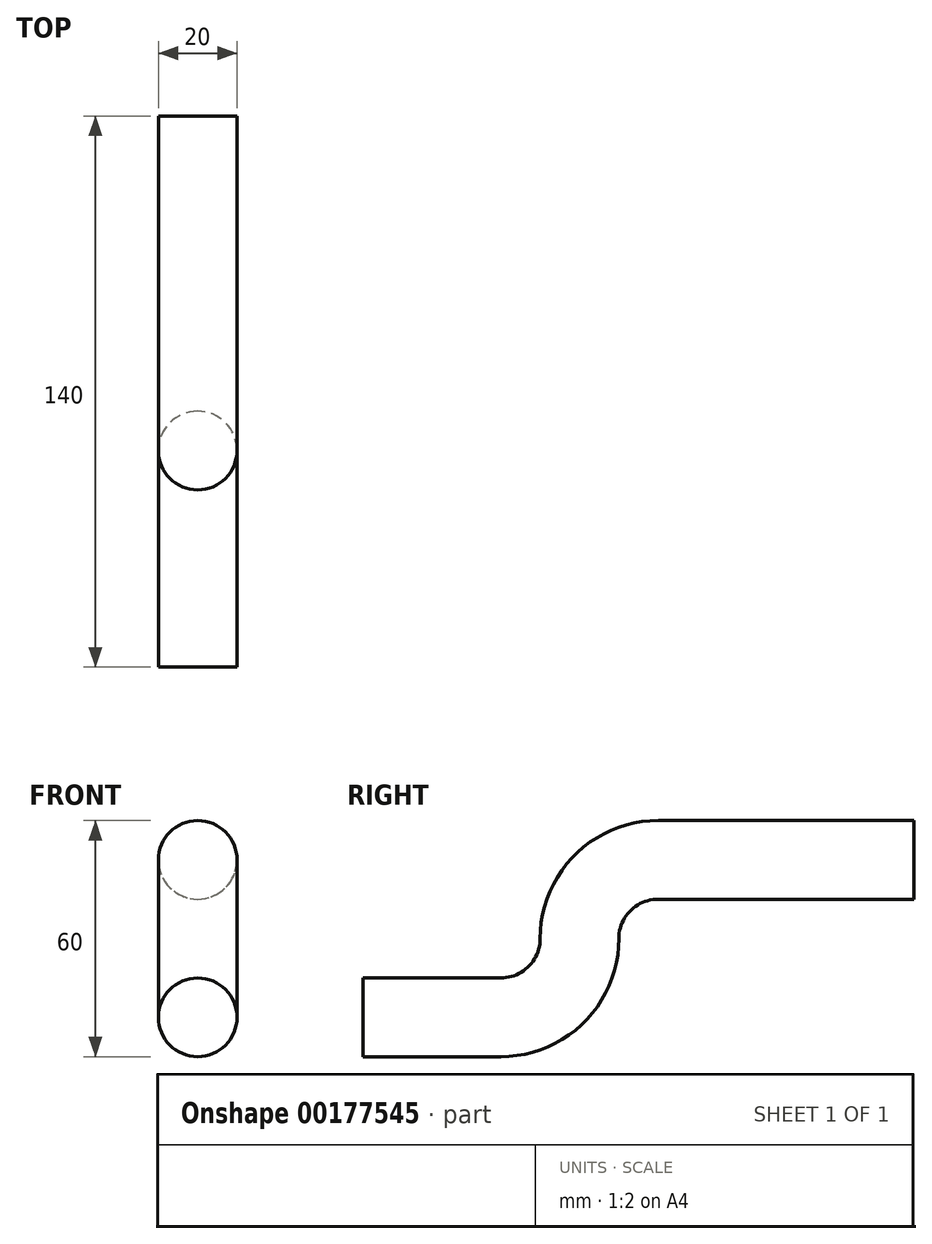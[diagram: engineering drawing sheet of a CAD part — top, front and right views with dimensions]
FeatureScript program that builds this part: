
annotation { "Feature Type Name" : "Feature", "Feature Type Description" : "" }
export const myFeature = defineFeature(function(context is Context, id is Id, definition is map)
    precondition{}
    {
        {
            var Q0;
            Q0=qCreatedBy(makeId("Front.planeOp"),FACE);
            var sketch = newSketch(context, id + "F0", { "sketchPlane" : qUnion([Q0])});
            skCircle(sketch, "E0", {"center": v(0, 0) * mm, "radius": 10 * mm});
            skSolve(sketch);
        }
        {
            var Q0;
            Q0=qCreatedBy(makeId("Right.planeOp"),FACE);
            var sketch = newSketch(context, id + "F1", { "sketchPlane" : qUnion([Q0])});
            skLineSegment(sketch, "E1", {"start": v(0, 0) * mm, "end": v(35, 0) * mm});
            skArc(sketch, "E2", {"start": v(35, 0) * mm, "mid": v(49.14, 5.86) * mm, "end": v(55, 20) * mm});
            skArc(sketch, "E3", {"start": v(55, 20) * mm, "mid": v(60.86, 34.14) * mm, "end": v(75, 40) * mm});
            skLineSegment(sketch, "E4", {"start": v(75, 40) * mm, "end": v(140, 40) * mm});
            skSolve(sketch);
        }
        {
            var Q0;
            Q0 = qSketchRegion(id + "F0", true);
            var Q1;
            Q1=sQuery(id+"F1.wireOp",EDGE,"E1");
            var Q2;
            Q2=sQuery(id+"F1.wireOp",EDGE,"E2");
            var Q3;
            Q3=sQuery(id+"F1.wireOp",EDGE,"E3");
            var Q4;
            Q4=sQuery(id+"F1.wireOp",EDGE,"E4");
            sweep(context, id + "F2", {"profiles" : qUnion([Q0]), "path" : qUnion([Q1, Q2, Q3, Q4])});
        }
    });
